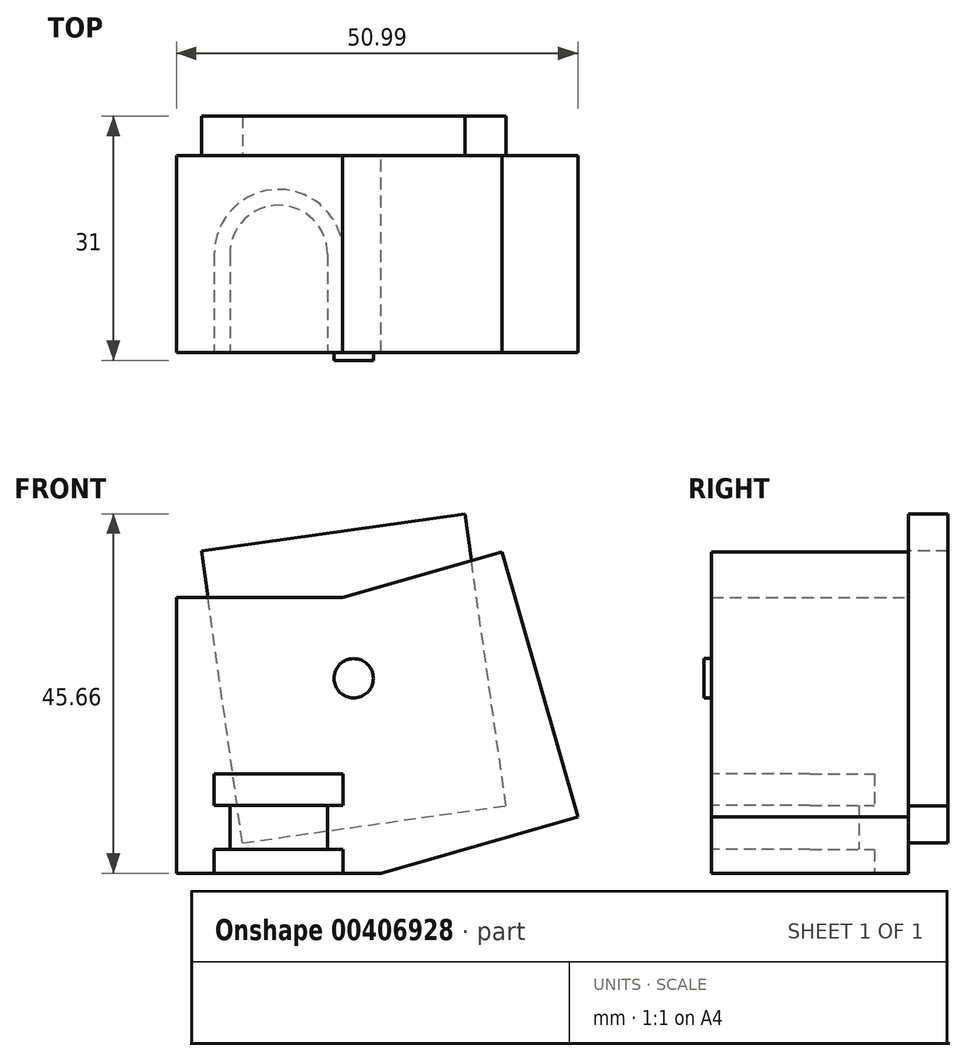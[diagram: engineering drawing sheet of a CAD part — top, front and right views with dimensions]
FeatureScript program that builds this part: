
annotation { "Feature Type Name" : "Feature", "Feature Type Description" : "" }
export const myFeature = defineFeature(function(context is Context, id is Id, definition is map)
    precondition{}
    {
        {
            var Q0;
            Q0=qCreatedBy(makeId("Front.planeOp"),FACE);
            var sketch = newSketch(context, id + "F0", { "sketchPlane" : qUnion([Q0])});
            skLineSegment(sketch, "E0", {"start": v(0, 68.4) * mm, "end": v(-14.95, -38) * mm, "construction": true});
            skLineSegment(sketch, "E1", {"start": v(-25.75, -21.38) * mm, "end": v(0, -25) * mm});
            skPoint(sketch, "E2", {"position": v(-12.87, -23.2) * mm});
            skLineSegment(sketch, "E3", {"start": v(-18.43, -5.24) * mm, "end": v(-2.59, -7.47) * mm, "construction": true});
            skPoint(sketch, "E4", {"position": v(-10.5, -6.36) * mm});
            skCircle(sketch, "E5", {"center": v(0, 0) * mm, "radius": 2.5 * mm});
            skLineSegment(sketch, "E6", {"start": v(2.23, 68.48) * mm, "end": v(-15.4, -56.98) * mm, "construction": true});
            skLineSegment(sketch, "E7", {"start": v(0, 0) * mm, "end": v(-9.43, 1.33) * mm, "construction": true});
            skLineSegment(sketch, "E8", {"start": v(-25.75, -21.38) * mm, "end": v(-20.88, 13.28) * mm});
            skLineSegment(sketch, "E9", {"start": v(-20.88, 13.28) * mm, "end": v(0, 10.34) * mm});
            skLineSegment(sketch, "E10.MirrorCS", {"start": v(25.75, -21.38) * mm, "end": v(0, -25) * mm});
            skLineSegment(sketch, "E11.MirrorCS", {"start": v(25.75, -21.38) * mm, "end": v(20.88, 13.28) * mm});
            skLineSegment(sketch, "E12.MirrorCS", {"start": v(20.88, 13.28) * mm, "end": v(0, 10.34) * mm});
            skSolve(sketch);
        }
        {
            var Q0;
            Q0 = qSketchRegion(id + "F0", true);
            extrude(context, id + "F1", {"entities" : qUnion([Q0]), "endBound" : BoundingType.SYMMETRIC, "depth" : 25 * mm});
        }
        {
            var Q0;
            Q0=makeQuery(id+"F1.opExtrude","SWEPT_FACE",FACE,{"disambiguationData":[OSD([sQuery(id+"F0.wireOp",EDGE,"E1")])]});
            var sketch = newSketch(context, id + "F2", { "sketchPlane" : qUnion([Q0])});
            skLineSegment(sketch, "E13", {"start": v(-22.52, 0) * mm, "end": v(3.48, 0) * mm, "construction": true});
            skCircle(sketch, "E14", {"center": v(-9.52, 0) * mm, "radius": 8.2 * mm});
            skLineSegment(sketch, "E15.bottom", {"start": v(-17.72, 0) * mm, "end": v(-1.32, 0) * mm});
            skLineSegment(sketch, "E15.top", {"start": v(-17.72, 12.5) * mm, "end": v(-1.32, 12.5) * mm});
            skLineSegment(sketch, "E15.left", {"start": v(-17.72, 0) * mm, "end": v(-17.72, 12.5) * mm});
            skLineSegment(sketch, "E15.right", {"start": v(-1.32, 0) * mm, "end": v(-1.32, 12.5) * mm});
            skSolve(sketch);
        }
        {
            var Q0;
            Q0 = qSketchRegion(id + "F2", true);
            extrude(context, id + "F3", {"entities" : qUnion([Q0]), "operationType" : NewBodyOperationType.REMOVE, "oppositeDirection" : true, "depth" : 3 * mm});
        }
        {
            var Q0;
            Q0=makeQuery(id+"F3.boolean.opBoolean","COPY",FACE,{"derivedFrom":makeQuery(id+"F3.opExtrude","CAP_FACE",FACE,{"disambiguationData":[OSD([sQuery(id+"F2.wireOp",EDGE,"E14"),sQuery(id+"F2.wireOp",EDGE,"E15.top"),sQuery(id+"F2.wireOp",EDGE,"E15.left"),sQuery(id+"F2.wireOp",EDGE,"E15.right")])],"isStart":false})});
            var sketch = newSketch(context, id + "F4", { "sketchPlane" : qUnion([Q0])});
            skCircle(sketch, "E16", {"center": v(-9.52, 0) * mm, "radius": 6.2 * mm});
            skLineSegment(sketch, "E17.bottom", {"start": v(-15.72, 0) * mm, "end": v(-3.32, 0) * mm});
            skLineSegment(sketch, "E17.top", {"start": v(-15.72, 12.5) * mm, "end": v(-3.32, 12.5) * mm});
            skLineSegment(sketch, "E17.left", {"start": v(-15.72, 0) * mm, "end": v(-15.72, 12.5) * mm});
            skLineSegment(sketch, "E17.right", {"start": v(-3.32, 0) * mm, "end": v(-3.32, 12.5) * mm});
            skSolve(sketch);
        }
        {
            var Q0;
            Q0 = qSketchRegion(id + "F4", true);
            extrude(context, id + "F5", {"entities" : qUnion([Q0]), "operationType" : NewBodyOperationType.REMOVE, "oppositeDirection" : true, "depth" : 5.6 * mm});
        }
        {
            var Q0;
            Q0=makeQuery(id+"F5.boolean.opBoolean","COPY",FACE,{"derivedFrom":makeQuery(id+"F5.opExtrude","CAP_FACE",FACE,{"disambiguationData":[OSD([sQuery(id+"F4.wireOp",EDGE,"E16"),sQuery(id+"F4.wireOp",EDGE,"E17.top"),sQuery(id+"F4.wireOp",EDGE,"E17.left"),sQuery(id+"F4.wireOp",EDGE,"E17.right")])],"isStart":false})});
            var sketch = newSketch(context, id + "F6", { "sketchPlane" : qUnion([Q0])});
            skCircle(sketch, "E18", {"center": v(-9.52, 0) * mm, "radius": 8.2 * mm});
            skLineSegment(sketch, "E19.bottom", {"start": v(-17.72, 0) * mm, "end": v(-1.32, 0) * mm});
            skLineSegment(sketch, "E19.top", {"start": v(-17.72, 12.5) * mm, "end": v(-1.32, 12.5) * mm});
            skLineSegment(sketch, "E19.left", {"start": v(-17.72, 0) * mm, "end": v(-17.72, 12.5) * mm});
            skLineSegment(sketch, "E19.right", {"start": v(-1.32, 0) * mm, "end": v(-1.32, 12.5) * mm});
            skSolve(sketch);
        }
        {
            var Q0;
            Q0 = qSketchRegion(id + "F6", true);
            extrude(context, id + "F7", {"entities" : qUnion([Q0]), "operationType" : NewBodyOperationType.REMOVE, "oppositeDirection" : true, "depth" : 4 * mm});
        }
        {
            var Q0;
            Q0=makeQuery(id+"F1.opExtrude","CAP_FACE",FACE,{"disambiguationData":[OSD([sQuery(id+"F0.wireOp",EDGE,"E1"),sQuery(id+"F0.wireOp",EDGE,"E5"),sQuery(id+"F0.wireOp",EDGE,"E8"),sQuery(id+"F0.wireOp",EDGE,"E9"),sQuery(id+"F0.wireOp",EDGE,"E10.MirrorCS"),sQuery(id+"F0.wireOp",EDGE,"E11.MirrorCS"),sQuery(id+"F0.wireOp",EDGE,"E12.MirrorCS")])],"isStart":true});
            var sketch = newSketch(context, id + "F8", { "sketchPlane" : qUnion([Q0])});
            skLineSegment(sketch, "E20.bottom", {"start": v(16.9, -18.73) * mm, "end": v(-16.9, -18.73) * mm});
            skLineSegment(sketch, "E20.top", {"start": v(16.9, 18.73) * mm, "end": v(-16.9, 18.73) * mm});
            skLineSegment(sketch, "E20.left", {"start": v(16.9, -18.73) * mm, "end": v(16.9, 18.73) * mm});
            skLineSegment(sketch, "E20.right", {"start": v(-16.9, -18.73) * mm, "end": v(-16.9, 18.73) * mm});
            skPoint(sketch, "E20.middle", {"position": v(0, 0) * mm});
            skSolve(sketch);
        }
        {
            var Q0;
            Q0 = qSketchRegion(id + "F8", true);
            extrude(context, id + "F9", {"entities" : qUnion([Q0]), "depth" : 5 * mm});
        }
        {
            var Q0;
            Q0=makeQuery(id+"F9.opExtrude","CAP_FACE",FACE,{"disambiguationData":[OSD([sQuery(id+"F8.wireOp",EDGE,"E20.bottom"),sQuery(id+"F8.wireOp",EDGE,"E20.top"),sQuery(id+"F8.wireOp",EDGE,"E20.left"),sQuery(id+"F8.wireOp",EDGE,"E20.right")])],"isStart":true});
            var sketch = newSketch(context, id + "F10", { "sketchPlane" : qUnion([Q0])});
            skCircle(sketch, "E21", {"center": v(0, 0) * mm, "radius": 2.5 * mm});
            skSolve(sketch);
        }
        {
            var Q0;
            Q0 = qSketchRegion(id + "F10", true);
            extrude(context, id + "F11", {"entities" : qUnion([Q0]), "operationType" : NewBodyOperationType.ADD, "depth" : 26 * mm});
        }
        {
            var Q0;
            Q0=makeQuery(id+"F1.opExtrude","SWEPT_BODY",BODY,{"disambiguationData":[OSD([sQuery(id+"F0.wireOp",EDGE,"E1"),sQuery(id+"F0.wireOp",EDGE,"E5"),sQuery(id+"F0.wireOp",EDGE,"E8"),sQuery(id+"F0.wireOp",EDGE,"E9"),sQuery(id+"F0.wireOp",EDGE,"E10.MirrorCS"),sQuery(id+"F0.wireOp",EDGE,"E11.MirrorCS"),sQuery(id+"F0.wireOp",EDGE,"E12.MirrorCS")])]});
            var Q1;
            Q1=makeQuery(id+"F11.opExtrude","CAP_EDGE",EDGE,{"disambiguationData":[OSD([sQuery(id+"F10.wireOp",EDGE,"E21")])],"isStart":false});
            transform(context, id + "F12", {"entities" : qUnion([Q0]), "transformType" : TransformType.ROTATION, "transformAxis" : qUnion([Q1]), "angle" : 8 * degree, "makeCopy" : false});
        }
    });
